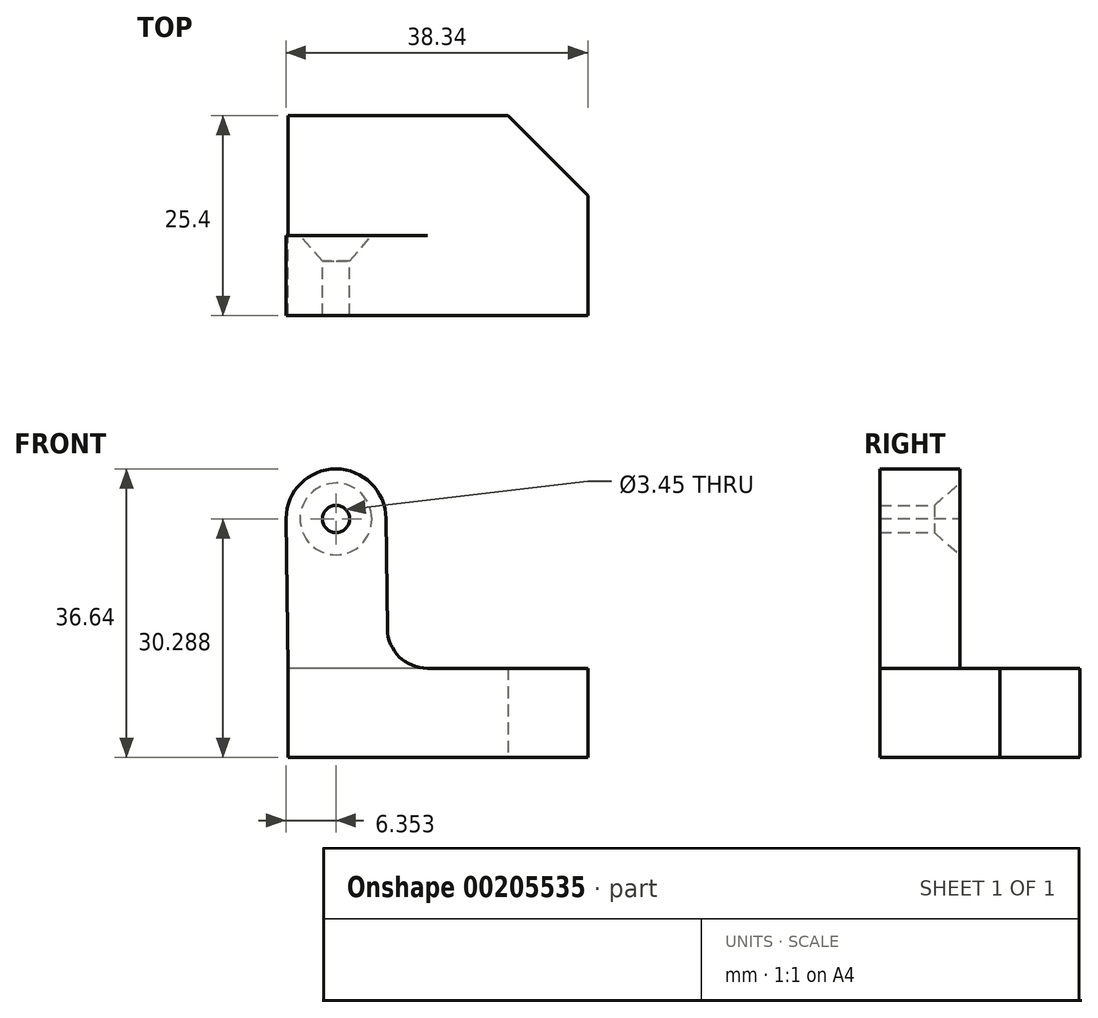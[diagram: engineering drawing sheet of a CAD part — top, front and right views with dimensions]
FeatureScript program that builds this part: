
annotation { "Feature Type Name" : "Feature", "Feature Type Description" : "" }
export const myFeature = defineFeature(function(context is Context, id is Id, definition is map)
    precondition{}
    {
        {
            var Q0;
            Q0=qCreatedBy(makeId("Front.planeOp"),FACE);
            var sketch = newSketch(context, id + "F0", { "sketchPlane" : qUnion([Q0])});
            skLineSegment(sketch, "E0.bottom", {"start": v(19.05, 5.66) * mm, "end": v(-19.05, 5.66) * mm});
            skLineSegment(sketch, "E0.top", {"start": v(19.05, -5.66) * mm, "end": v(-19.05, -5.66) * mm});
            skLineSegment(sketch, "E0.left", {"start": v(19.05, 5.66) * mm, "end": v(19.05, -5.66) * mm});
            skLineSegment(sketch, "E0.right", {"start": v(-19.05, 5.66) * mm, "end": v(-19.05, -5.66) * mm});
            skPoint(sketch, "E0.middle", {"position": v(0, 0) * mm});
            skLineSegment(sketch, "E1", {"start": v(-6.59, 24.7) * mm, "end": v(-6.35, 5.66) * mm});
            skArc(sketch, "E2", {"start": v(-6.59, 24.7) * mm, "mid": v(-12.94, 30.98) * mm, "end": v(-19.29, 24.7) * mm});
            skLineSegment(sketch, "E3", {"start": v(-19.29, 24.7) * mm, "end": v(-19.05, 5.66) * mm});
            skSolve(sketch);
        }
        {
            var Q0;
            Q0 = qSketchRegion(id + "F0", true);
            extrude(context, id + "F1", {"entities" : qUnion([Q0]), "depth" : 25.4 * mm});
        }
        {
            var Q0;
            {var subQ2=sQuery(id+"F0.wireOp",EDGE,"E1");Q0=makeQuery(id+"F0.imprint","IMPRINT",FACE,{"disambiguationData":[TD([[makeQuery(id+"F0.imprint","IMPRINT",EDGE,{"derivedFrom":subQ2}),-1.0]])]});}
            extrude(context, id + "F2", {"entities" : qUnion([Q0]), "operationType" : NewBodyOperationType.REMOVE, "depth" : 15.24 * mm});
        }
        {
            var Q0;
            Q0=sQuery(id+"F0.wireOp",VERTEX,"E2.center");
            var Q1;
            Q1=makeQuery(id+"F1.opExtrude","SWEPT_BODY",BODY,{"disambiguationData":[OSD([sQuery(id+"F0.wireOp",EDGE,"E0.bottom"),sQuery(id+"F0.wireOp",EDGE,"E0.top"),sQuery(id+"F0.wireOp",EDGE,"E0.left"),sQuery(id+"F0.wireOp",EDGE,"E0.right"),sQuery(id+"F0.wireOp",EDGE,"E1"),sQuery(id+"F0.wireOp",EDGE,"E2"),sQuery(id+"F0.wireOp",EDGE,"E3")])]});
            hole(context, id + "F3", {"style" : HoleStyle.C_SINK, "endStyle" : HoleEndStyle.THROUGH, "oppositeDirection" : true, "standardTappedOrClearance" : lookupTablePath({ "standard" : "ANSI", "engagement" : "75%", "pitch" : "32 tpi", "size" : "#8", "type" : "Tapped" }), "standardBlindInLast" : lookupTablePath({ "standard" : "ANSI", "engagement" : "75%", "pitch" : "32 tpi", "size" : "#8", "type" : "Tapped" }), "holeDiameter" : 3.45 * mm, "cSinkDiameter" : 9.12 * mm, "cSinkAngle" : 82 * degree, "locations" : qUnion([Q0]), "scope" : qUnion([Q1]), "isTappedThrough" : true, "majorDiameter" : 4.17 * mm, "showTappedDepth" : true});
        }
        {
            var Q0;
            Q0=makeQuery(id+"F1.opExtrude","SWEPT_EDGE",EDGE,{"disambiguationData":[OSD([sQuery(id+"F0.wireOp",EDGE,"E0.bottom"),sQuery(id+"F0.wireOp",EDGE,"E1")])]});
            fillet(context, id + "F4", {"entities" : qUnion([Q0]), "radius" : 5.08 * mm, "tangentPropagation" : true, "allowEdgeOverflow" : false});
        }
        {
            var Q0;
            Q0=makeQuery(id+"F1.opExtrude","CAP_EDGE",EDGE,{"disambiguationData":[OSD([sQuery(id+"F0.wireOp",EDGE,"E0.left")])],"isStart":true});
            chamfer(context, id + "F5", {"entities" : qUnion([Q0]), "width" : 10.16 * mm, "tangentPropagation" : true});
        }
    });
